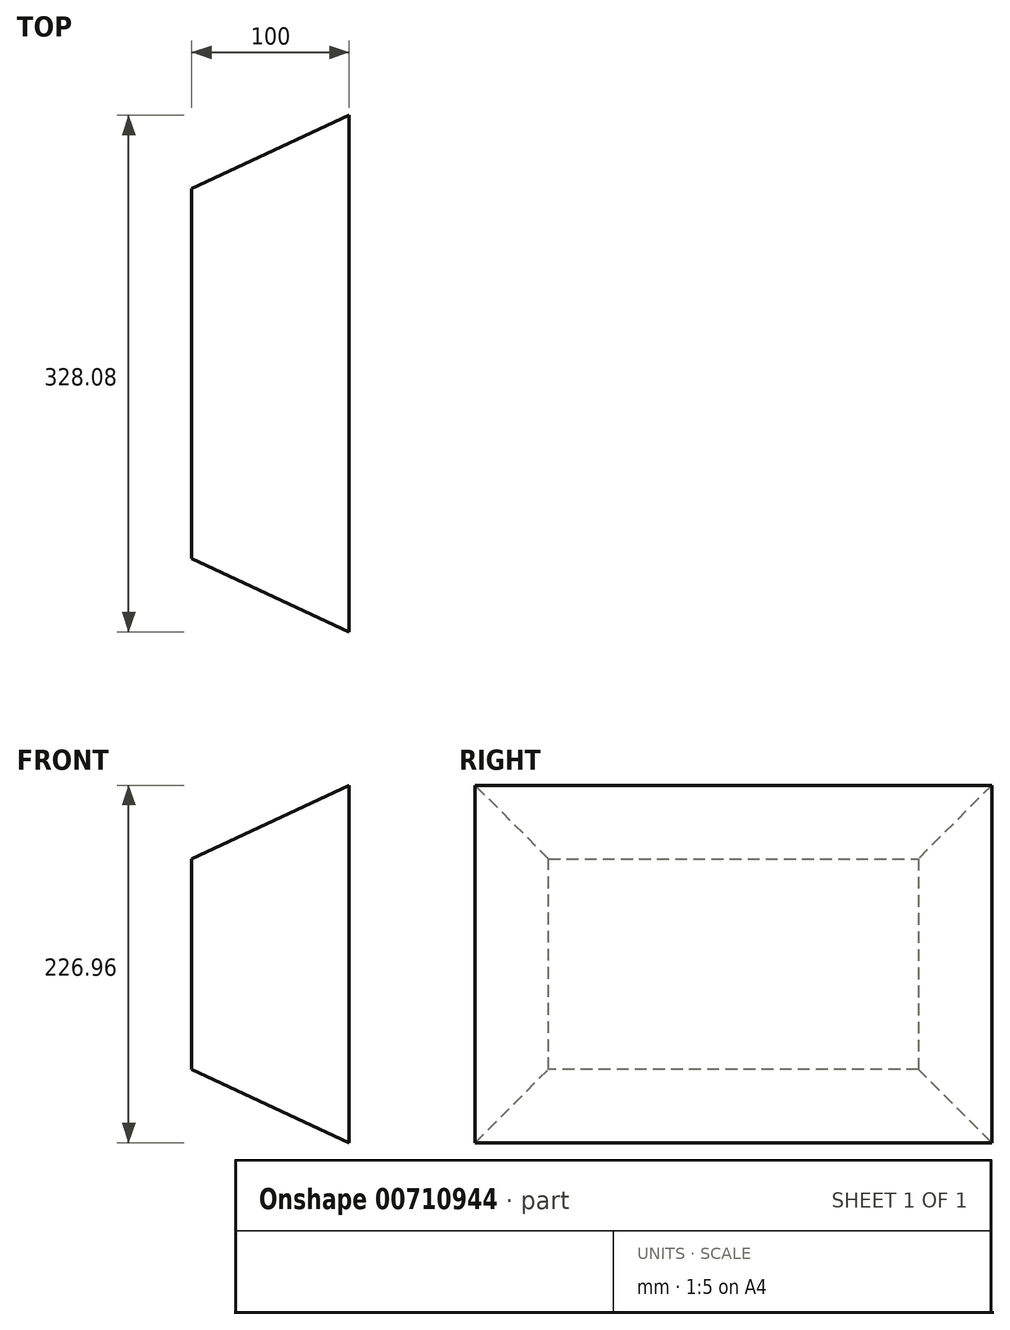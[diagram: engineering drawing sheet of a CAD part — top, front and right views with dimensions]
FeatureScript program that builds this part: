
annotation { "Feature Type Name" : "Feature", "Feature Type Description" : "" }
export const myFeature = defineFeature(function(context is Context, id is Id, definition is map)
    precondition{}
    {
        {
            var Q0;
            Q0=qCreatedBy(makeId("Right.planeOp"),FACE);
            var sketch = newSketch(context, id + "F0", { "sketchPlane" : qUnion([Q0])});
            skLineSegment(sketch, "E0.bottom", {"start": v(0, 0) * mm, "end": v(0, 0) * mm});
            skLineSegment(sketch, "E0.top", {"start": v(0, 0) * mm, "end": v(0, 0) * mm});
            skLineSegment(sketch, "E0.left", {"start": v(0, 0) * mm, "end": v(0, 0) * mm});
            skLineSegment(sketch, "E0.right", {"start": v(0, 0) * mm, "end": v(0, 0) * mm});
            skPoint(sketch, "E0.middle", {"position": v(0, 0) * mm});
            skLineSegment(sketch, "E1.bottom", {"start": v(-117.4, 66.85) * mm, "end": v(117.4, 66.85) * mm});
            skLineSegment(sketch, "E1.top", {"start": v(-117.4, -66.85) * mm, "end": v(117.4, -66.85) * mm});
            skLineSegment(sketch, "E1.left", {"start": v(-117.4, 66.85) * mm, "end": v(-117.4, -66.85) * mm});
            skLineSegment(sketch, "E1.right", {"start": v(117.4, 66.85) * mm, "end": v(117.4, -66.85) * mm});
            skSolve(sketch);
        }
        {
            var Q0;
            Q0 = qSketchRegion(id + "F0", true);
            extrude(context, id + "F1", {"entities" : qUnion([Q0]), "depth" : 100 * mm, "offsetDistance" : 25.4 * mm, "hasDraft" : true, "draftAngle" : 25 * degree});
        }
    });
